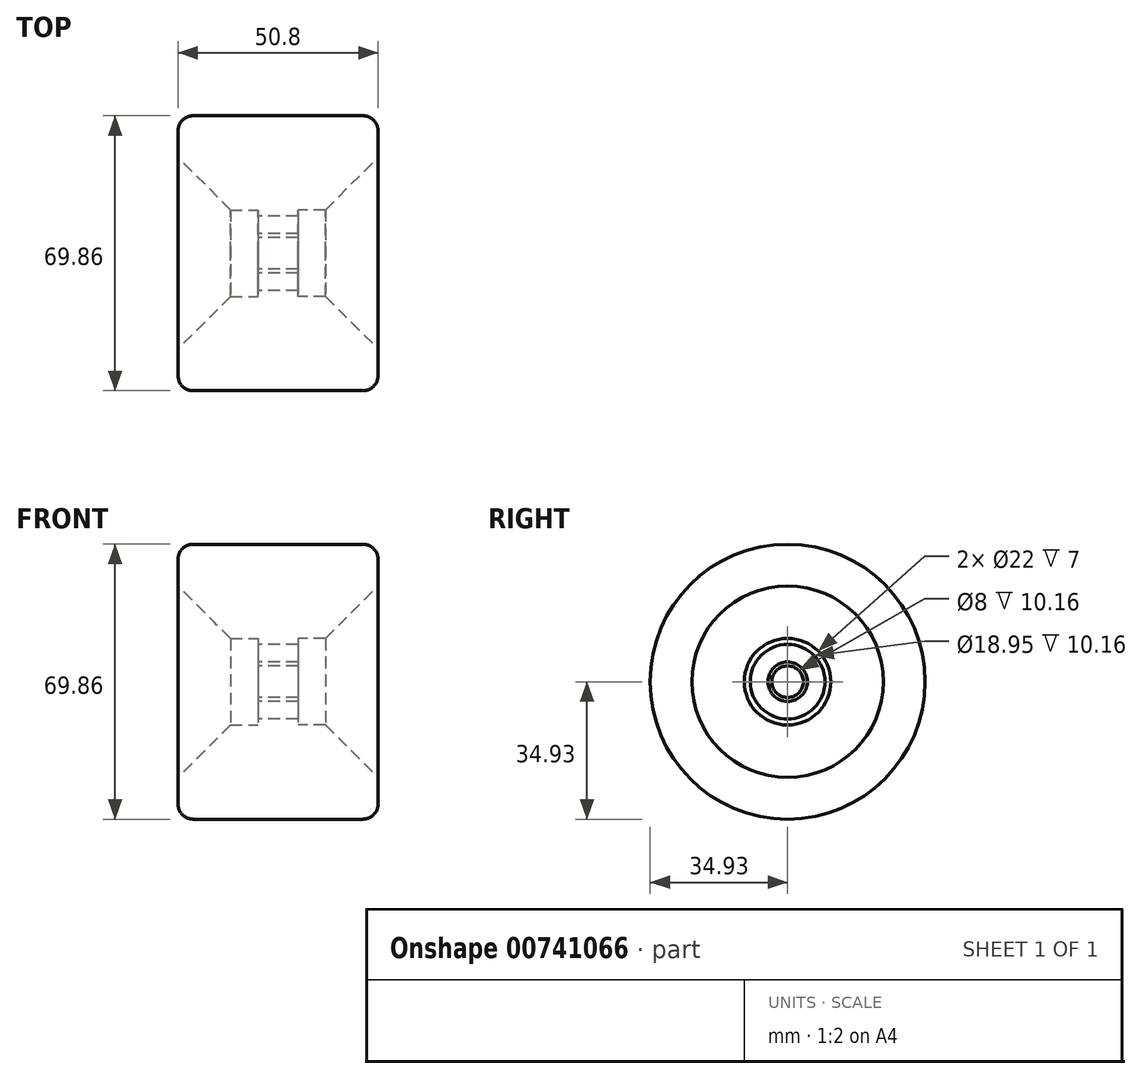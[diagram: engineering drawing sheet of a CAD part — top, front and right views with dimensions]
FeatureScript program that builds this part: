
annotation { "Feature Type Name" : "Feature", "Feature Type Description" : "" }
export const myFeature = defineFeature(function(context is Context, id is Id, definition is map)
    precondition{}
    {
        {
            var Q0;
            Q0=qCreatedBy(makeId("Front.planeOp"),FACE);
            var sketch = newSketch(context, id + "F0", { "sketchPlane" : qUnion([Q0])});
            skLineSegment(sketch, "E0", {"start": v(0, 9.48) * mm, "end": v(0, 34.93) * mm});
            skLineSegment(sketch, "E1", {"start": v(0, 34.93) * mm, "end": v(21.59, 34.93) * mm});
            skLineSegment(sketch, "E2", {"start": v(25.4, 31.12) * mm, "end": v(25.4, 24.32) * mm});
            skLineSegment(sketch, "E3", {"start": v(25.4, 24.32) * mm, "end": v(12.08, 11) * mm});
            skLineSegment(sketch, "E4", {"start": v(12.08, 11) * mm, "end": v(5.08, 11) * mm});
            skLineSegment(sketch, "E5", {"start": v(5.08, 11) * mm, "end": v(5.08, 9.48) * mm});
            skLineSegment(sketch, "E6", {"start": v(5.08, 9.48) * mm, "end": v(0, 9.48) * mm});
            skLineSegment(sketch, "E7", {"start": v(0, 9.48) * mm, "end": v(0, 0) * mm, "construction": true});
            skLineSegment(sketch, "E8", {"start": v(0, 0) * mm, "end": v(41.5, 0) * mm, "construction": true});
            skPoint(sketch, "E9.visualSharp", {"position": v(25.4, 34.93) * mm});
            skArc(sketch, "E9.filletArc", {"start": v(25.4, 31.12) * mm, "mid": v(24.28, 33.8) * mm, "end": v(21.59, 34.93) * mm});
            skSolve(sketch);
        }
        {
            var Q0;
            Q0 = qSketchRegion(id + "F0", true);
            var Q1;
            Q1=sQuery(id+"F0.wireOp",EDGE,"E8");
            revolve(context, id + "F1", {"surfaceOperationType" : NewSurfaceOperationType.NEW, "entities" : qUnion([Q0]), "axis" : qUnion([Q1]), "revolveType" : RevolveType.FULL});
        }
        {
            var Q0;
            Q0=makeQuery(id+"F1.opRevolve","SWEPT_BODY",BODY,{"disambiguationData":[OSD([sQuery(id+"F0.wireOp",EDGE,"E0"),sQuery(id+"F0.wireOp",EDGE,"E1"),sQuery(id+"F0.wireOp",EDGE,"E2"),sQuery(id+"F0.wireOp",EDGE,"E3"),sQuery(id+"F0.wireOp",EDGE,"E4"),sQuery(id+"F0.wireOp",EDGE,"E5"),sQuery(id+"F0.wireOp",EDGE,"E6"),sQuery(id+"F0.wireOp",EDGE,"E9.filletArc")])]});
            var Q1;
            Q1=makeQuery(id+"F1.opRevolve","SWEPT_FACE",FACE,{"disambiguationData":[OSD([sQuery(id+"F0.wireOp",EDGE,"E0")])]});
            mirror(context, id + "F2", {"operationType" : NewBodyOperationType.ADD, "entities" : qUnion([Q0]), "mirrorPlane" : qUnion([Q1])});
        }
        {
            var Q0;
            Q0=qCreatedBy(makeId("Front.planeOp"),FACE);
            var sketch = newSketch(context, id + "F3", { "sketchPlane" : qUnion([Q0])});
            skLineSegment(sketch, "E10.bottom", {"start": v(-5.08, 5.02) * mm, "end": v(5.08, 5.02) * mm});
            skLineSegment(sketch, "E10.top", {"start": v(-5.08, 4) * mm, "end": v(5.08, 4) * mm});
            skLineSegment(sketch, "E10.left", {"start": v(-5.08, 5.02) * mm, "end": v(-5.08, 4) * mm});
            skLineSegment(sketch, "E10.right", {"start": v(5.08, 5.02) * mm, "end": v(5.08, 4) * mm});
            skSolve(sketch);
        }
        {
            var Q0;
            Q0 = qSketchRegion(id + "F3", true);
            var Q1;
            Q1=sQuery(id+"F0.wireOp",EDGE,"E8");
            revolve(context, id + "F4", {"surfaceOperationType" : NewSurfaceOperationType.NEW, "entities" : qUnion([Q0]), "axis" : qUnion([Q1]), "revolveType" : RevolveType.FULL});
        }
    });
